# Revit family: Casement_38_E_Side_Hung_Standard
name_source: partatom
category: Windows
revit_build: Autodesk Revit 2014 (Build: 20130308_1515(x64)
units: mm (PartAtom-declared; Revit-internal decimal feet)

## types (18) — shared parameters
Aluminium Thickness = 1 mm  [stored 0.00328084 ft]
Area Pane Left Top = 0.52 m²
Bead SG Gap = 13 mm  [stored 0.0426509 ft]
Casement Dimension = 38 mm  [stored 0.124672 ft]
Custom Sash Height = 1154 mm  [stored 3.78609 ft]
Custom Sash Width = 554 mm  [stored 1.81759 ft]
DG Extrusion Start = 9 mm  [stored 0.0295276 ft]
DG Gasket Finish = Double Glazing Gasket Material
DG Thickness Calc = 4 mm  [stored 0.0131234 ft]
Default Sill Height = 800 mm  [stored 2.62467 ft]
Depth Bead = 24 mm  [stored 0.0787402 ft]
Description = Window 38mm, Type E side hung
Frame Center Offset = 19 mm  [stored 0.062336 ft]
Height Panel 1 = 1139 mm  [stored 3.73688 ft]
Height Sash = 1124 mm  [stored 3.68766 ft]
Height Sash Opening = 1154 mm  [stored 3.78609 ft]
Length Transom = 540 mm  [stored 1.77165 ft]
Limit Fixed Pane Height Max = 1800 mm
Limit Fixed Pane Height Min = 200 mm  [stored 0.656168 ft]
Limit Fixed Pane Width Max = 1500 mm
Limit Fixed Pane Width Min = 200 mm  [stored 0.656168 ft]
Limit Sash Height Max = 1500 mm
Limit Sash Height Min = 300 mm  [stored 0.984252 ft]
Limit Sash Width Max = 700 mm  [stored 2.29659 ft]
Limit Sash Width Min = 300 mm  [stored 0.984252 ft]
Limit Window Height Max = 1860 mm
Limit Window Height Min = 1430 mm
Limit Window Width Max = 2130 mm
Limit Window Width Min = 830 mm  [stored 2.7231 ft]
Manufacturer = Crealco
Max System DG One Piece Thickness = 6 mm  [stored 0.019685 ft]
Max System DG Unit Thickness = 25 mm  [stored 0.082021 ft]
Model = Casement 38
Offset Bead SG Center Reversed = 19 mm  [stored 0.062336 ft]
Offset Mullion Left = 570 mm  [stored 1.87008 ft]
Offset Panel 3 Bead Top = 1200 mm
Offset Panel 4 Left = 600 mm  [stored 1.9685 ft]
Offset Sash Left = 23 mm  [stored 0.0754593 ft]
Offset Sash Top = 23 mm  [stored 0.0754593 ft]
Offset Transom Top = 1170 mm
Offset Window Exterior = 19 mm  [stored 0.062336 ft]
SG Gasket Thickness = 6 mm  [stored 0.019685 ft]
Sash Center Offset = 16 mm  [stored 0.0524934 ft]
Sash Overlap = 7 mm  [stored 0.0229659 ft]
Sash Spacing Inner = 8 mm  [stored 0.0262467 ft]
URL = http://www.crealco.co.za
Wall Closure = By host
Width Bead = 15 mm  [stored 0.0492126 ft]
Width Fixed Pane Bottom LHS = 540 mm  [stored 1.77165 ft]
Width Panel 1 = 540 mm  [stored 1.77165 ft]
Width Profile = 30 mm  [stored 0.0984252 ft]
Width Sash = 524 mm  [stored 1.71916 ft]
Width Sash Opening = 554 mm  [stored 1.81759 ft]
zero-valued in all types: Window Exterior Offset

## per-type parameters (varying)
- 38-0915S-1000Pa: Area Pane Left Bottom=0.13 m²; Area Pane Right=0.36 m²; Clearvue Insulated LowE SHGC Value=0.51; Clearvue Insulated LowE U Value=3.91; Clearvue Insulated SHGC Value=0.56; Clearvue Insulated U Value=4.43; Clearvue SHGC Value=0.641; Clearvue U Value=6.69; Custom Windload=1000 mm  [stored 3.28084 ft]; Custom Window Height=1490 mm; Custom Window Width=890 mm  [stored 2.91995 ft]; Depth Mullion=39 mm  [stored 0.127953 ft]; Energy Advantage SHGC Value=0.576; Energy Advantage U Value=5.11; Height=1490 mm; Height Fixed Pane Bottom LHS=260 mm  [stored 0.853018 ft]; Height Fixed Pane RHS=1430 mm; Intruderprufe Insulated LowE SHGC Value=0.474; Intruderprufe Insulated LowE U Value=3.82; Intruderprufe Insulated SHGC Value=0.519; Intruderprufe Insulated U Value=4.32; Intruderprufe LowE SHGC Value=0.53; Intruderprufe LowE U Value=4.98; Intruderprufe SHGC Value=0.628; Intruderprufe U Value=6.75; Length Mullion=1490 mm; Max Pane Area=0.52 m²; Mullion Depth Windload Based=39 mm  [stored 0.127953 ft]; Width=890 mm  [stored 2.91995 ft]; Width Fixed Pane RHS=260 mm  [stored 0.853018 ft]; Windload Design=1000 mm  [stored 3.28084 ft]
- 38-0915S-1500Pa: Area Pane Left Bottom=0.13 m²; Area Pane Right=0.36 m²; Clearvue Insulated LowE SHGC Value=0.511; Clearvue Insulated LowE U Value=3.98; Clearvue Insulated SHGC Value=0.561; Clearvue Insulated U Value=45; Clearvue SHGC Value=0.64; Clearvue U Value=6.69; Custom Windload=1500 mm; Custom Window Height=1490 mm; Custom Window Width=890 mm  [stored 2.91995 ft]; Depth Mullion=54 mm  [stored 0.177165 ft]; Energy Advantage SHGC Value=0.574; Energy Advantage U Value=5.2; Height=1490 mm; Height Fixed Pane Bottom LHS=260 mm  [stored 0.853018 ft]; Height Fixed Pane RHS=1430 mm; Intruderprufe Insulated LowE SHGC Value=0.476; Intruderprufe Insulated LowE U Value=3.89; Intruderprufe Insulated SHGC Value=0.522; Intruderprufe Insulated U Value=4.39; Intruderprufe LowE SHGC Value=0.541; Intruderprufe LowE U Value=5.07; Intruderprufe SHGC Value=0.61; Intruderprufe U Value=6.59; Length Mullion=1490 mm; Max Pane Area=0.52 m²; Mullion Depth Windload Based=54 mm  [stored 0.177165 ft]; Width=890 mm  [stored 2.91995 ft]; Width Fixed Pane RHS=260 mm  [stored 0.853018 ft]; Windload Design=1500 mm
- 38-0915S-2000Pa: Area Pane Left Bottom=0.13 m²; Area Pane Right=0.36 m²; Clearvue Insulated LowE SHGC Value=0.511; Clearvue Insulated LowE U Value=3.98; Clearvue Insulated SHGC Value=0.561; Clearvue Insulated U Value=45; Clearvue SHGC Value=0.64; Clearvue U Value=6.69; Custom Windload=2000 mm; Custom Window Height=1490 mm; Custom Window Width=890 mm  [stored 2.91995 ft]; Depth Mullion=54 mm  [stored 0.177165 ft]; Energy Advantage SHGC Value=0.574; Energy Advantage U Value=5.2; Height=1490 mm; Height Fixed Pane Bottom LHS=260 mm  [stored 0.853018 ft]; Height Fixed Pane RHS=1430 mm; Intruderprufe Insulated LowE SHGC Value=0.476; Intruderprufe Insulated LowE U Value=3.89; Intruderprufe Insulated SHGC Value=0.522; Intruderprufe Insulated U Value=4.39; Intruderprufe LowE SHGC Value=0.541; Intruderprufe LowE U Value=5.07; Intruderprufe SHGC Value=0.61; Intruderprufe U Value=6.59; Length Mullion=1490 mm; Max Pane Area=0.52 m²; Mullion Depth Windload Based=54 mm  [stored 0.177165 ft]; Width=890 mm  [stored 2.91995 ft]; Width Fixed Pane RHS=260 mm  [stored 0.853018 ft]; Windload Design=2000 mm
- 38-1215S-1000Pa: Area Pane Left Bottom=0.13 m²; Area Pane Right=0.78 m²; Clearvue Insulated LowE SHGC Value=0.575; Clearvue Insulated LowE U Value=3.67; Clearvue Insulated SHGC Value=0.632; Clearvue Insulated U Value=4.28; Clearvue SHGC Value=0.722; Clearvue U Value=6.86; Custom Windload=1000 mm  [stored 3.28084 ft]; Custom Window Height=1490 mm; Custom Window Width=1190 mm  [stored 3.9042 ft]; Depth Mullion=39 mm  [stored 0.127953 ft]; Energy Advantage SHGC Value=0.647; Energy Advantage U Value=5.06; Height=1490 mm; Height Fixed Pane Bottom LHS=260 mm  [stored 0.853018 ft]; Height Fixed Pane RHS=1430 mm; Intruderprufe Insulated LowE SHGC Value=0.532; Intruderprufe Insulated LowE U Value=3.59; Intruderprufe Insulated SHGC Value=0.585; Intruderprufe Insulated U Value=4.18; Intruderprufe LowE SHGC Value=0.604; Intruderprufe LowE U Value=4.94; Intruderprufe SHGC Value=0.698; Intruderprufe U Value=6.73; Length Mullion=1490 mm; Max Pane Area=0.78 m²; Mullion Depth Windload Based=39 mm  [stored 0.127953 ft]; Width=1190 mm  [stored 3.9042 ft]; Width Fixed Pane RHS=560 mm; Windload Design=1000 mm  [stored 3.28084 ft]
- 38-1215S-1500Pa: Area Pane Left Bottom=0.13 m²; Area Pane Right=0.78 m²; Clearvue Insulated LowE SHGC Value=0.575; Clearvue Insulated LowE U Value=3.75; Clearvue Insulated SHGC Value=0.632; Clearvue Insulated U Value=4.34; Clearvue SHGC Value=0.721; Clearvue U Value=6.85; Custom Windload=1500 mm; Custom Window Height=1490 mm; Custom Window Width=1190 mm  [stored 3.9042 ft]; Depth Mullion=54 mm  [stored 0.177165 ft]; Energy Advantage SHGC Value=0.645; Energy Advantage U Value=5.13; Height=1490 mm; Height Fixed Pane Bottom LHS=260 mm  [stored 0.853018 ft]; Height Fixed Pane RHS=1430 mm; Intruderprufe Insulated LowE SHGC Value=0.534; Intruderprufe Insulated LowE U Value=3.65; Intruderprufe Insulated SHGC Value=0.587; Intruderprufe Insulated U Value=4.23; Intruderprufe LowE SHGC Value=0.606; Intruderprufe LowE U Value=5.01; Intruderprufe SHGC Value=0.685; Intruderprufe U Value=6.75; Length Mullion=1490 mm; Max Pane Area=0.78 m²; Mullion Depth Windload Based=54 mm  [stored 0.177165 ft]; Width=1190 mm  [stored 3.9042 ft]; Width Fixed Pane RHS=560 mm; Windload Design=1500 mm
- 38-1215S-2000Pa: Area Pane Left Bottom=0.13 m²; Area Pane Right=0.78 m²; Clearvue Insulated LowE SHGC Value=0.575; Clearvue Insulated LowE U Value=3.75; Clearvue Insulated SHGC Value=0.632; Clearvue Insulated U Value=4.34; Clearvue SHGC Value=0.721; Clearvue U Value=6.85; Custom Windload=2000 mm; Custom Window Height=1490 mm; Custom Window Width=1190 mm  [stored 3.9042 ft]; Depth Mullion=54 mm  [stored 0.177165 ft]; Energy Advantage SHGC Value=0.645; Energy Advantage U Value=5.13; Height=1490 mm; Height Fixed Pane Bottom LHS=260 mm  [stored 0.853018 ft]; Height Fixed Pane RHS=1430 mm; Intruderprufe Insulated LowE SHGC Value=0.534; Intruderprufe Insulated LowE U Value=3.65; Intruderprufe Insulated SHGC Value=0.587; Intruderprufe Insulated U Value=4.23; Intruderprufe LowE SHGC Value=0.606; Intruderprufe LowE U Value=5.01; Intruderprufe SHGC Value=0.685; Intruderprufe U Value=6.75; Length Mullion=1490 mm; Max Pane Area=0.78 m²; Mullion Depth Windload Based=54 mm  [stored 0.177165 ft]; Width=1190 mm  [stored 3.9042 ft]; Width Fixed Pane RHS=560 mm; Windload Design=2000 mm
- 38-1515S-1000Pa: Area Pane Left Bottom=0.13 m²; Area Pane Right=1.21 m²; Clearvue Insulated LowE SHGC Value=0.616; Clearvue Insulated LowE U Value=3.51; Clearvue Insulated SHGC Value=0.677; Clearvue Insulated U Value=4.19; Clearvue SHGC Value=0.772; Clearvue U Value=6.96; Custom Windload=1000 mm  [stored 3.28084 ft]; Custom Window Height=1490 mm; Custom Window Width=1490 mm; Depth Mullion=39 mm  [stored 0.127953 ft]; Energy Advantage SHGC Value=0.692; Energy Advantage U Value=5.03; Height=1490 mm; Height Fixed Pane Bottom LHS=260 mm  [stored 0.853018 ft]; Height Fixed Pane RHS=1430 mm; Intruderprufe Insulated LowE SHGC Value=0.569; Intruderprufe Insulated LowE U Value=3.44; Intruderprufe Insulated SHGC Value=0.626; Intruderprufe Insulated U Value=4.09; Intruderprufe LowE SHGC Value=0.646; Intruderprufe LowE U Value=4.91; Intruderprufe SHGC Value=0.743; Intruderprufe U Value=6.83; Length Mullion=1490 mm; Max Pane Area=1.21 m²; Mullion Depth Windload Based=39 mm  [stored 0.127953 ft]; Width=1490 mm; Width Fixed Pane RHS=860 mm  [stored 2.82152 ft]; Windload Design=1000 mm  [stored 3.28084 ft]
- 38-1515S-1500Pa: Area Pane Left Bottom=0.13 m²; Area Pane Right=1.21 m²; Clearvue Insulated LowE SHGC Value=0.616; Clearvue Insulated LowE U Value=3.56; Clearvue Insulated SHGC Value=0.677; Clearvue Insulated U Value=4.23; Clearvue SHGC Value=0.772; Clearvue U Value=6.69; Custom Windload=1500 mm; Custom Window Height=1490 mm; Custom Window Width=1490 mm; Depth Mullion=54 mm  [stored 0.177165 ft]; Energy Advantage SHGC Value=0.691; Energy Advantage U Value=5.09; Height=1490 mm; Height Fixed Pane Bottom LHS=260 mm  [stored 0.853018 ft]; Height Fixed Pane RHS=1430 mm; Intruderprufe Insulated LowE SHGC Value=0.57; Intruderprufe Insulated LowE U Value=3.49; Intruderprufe Insulated SHGC Value=0.629; Intruderprufe Insulated U Value=4.13; Intruderprufe LowE SHGC Value=0.647; Intruderprufe LowE U Value=4.97; Intruderprufe SHGC Value=0.732; Intruderprufe U Value=6.84; Length Mullion=1490 mm; Max Pane Area=1.21 m²; Mullion Depth Windload Based=54 mm  [stored 0.177165 ft]; Width=1490 mm; Width Fixed Pane RHS=860 mm  [stored 2.82152 ft]; Windload Design=1500 mm
- 38-1515S-2000Pa: Area Pane Left Bottom=0.13 m²; Area Pane Right=1.21 m²; Clearvue Insulated LowE SHGC Value=0.616; Clearvue Insulated LowE U Value=3.56; Clearvue Insulated SHGC Value=0.677; Clearvue Insulated U Value=4.23; Clearvue SHGC Value=0.772; Clearvue U Value=6.69; Custom Windload=2000 mm; Custom Window Height=1490 mm; Custom Window Width=1490 mm; Depth Mullion=54 mm  [stored 0.177165 ft]; Energy Advantage SHGC Value=0.691; Energy Advantage U Value=5.09; Height=1490 mm; Height Fixed Pane Bottom LHS=260 mm  [stored 0.853018 ft]; Height Fixed Pane RHS=1430 mm; Intruderprufe Insulated LowE SHGC Value=0.57; Intruderprufe Insulated LowE U Value=3.49; Intruderprufe Insulated SHGC Value=0.629; Intruderprufe Insulated U Value=4.13; Intruderprufe LowE SHGC Value=0.647; Intruderprufe LowE U Value=4.97; Intruderprufe SHGC Value=0.732; Intruderprufe U Value=6.84; Length Mullion=1490 mm; Max Pane Area=1.21 m²; Mullion Depth Windload Based=54 mm  [stored 0.177165 ft]; Width=1490 mm; Width Fixed Pane RHS=860 mm  [stored 2.82152 ft]; Windload Design=2000 mm
- 38-0918S-1000Pa: Area Pane Left Bottom=0.29 m²; Area Pane Right=0.43 m²; Clearvue Insulated LowE SHGC Value=0.55; Clearvue Insulated LowE U Value=4.07; Clearvue Insulated SHGC Value=0.604; Clearvue Insulated U Value=4.64; Clearvue SHGC Value=0.688; Clearvue U Value=7; Custom Windload=1000 mm  [stored 3.28084 ft]; Custom Window Height=1790 mm; Custom Window Width=890 mm  [stored 2.91995 ft]; Depth Mullion=54 mm  [stored 0.177165 ft]; Energy Advantage SHGC Value=0.617; Energy Advantage U Value=5.38; Height=1790 mm; Height Fixed Pane Bottom LHS=560 mm; Height Fixed Pane RHS=1730 mm; Intruderprufe Insulated LowE SHGC Value=0.512; Intruderprufe Insulated LowE U Value=3.98; Intruderprufe Insulated SHGC Value=0.562; Intruderprufe Insulated U Value=4.52; Intruderprufe LowE SHGC Value=0.581; Intruderprufe LowE U Value=5.25; Intruderprufe SHGC Value=0.655; Intruderprufe U Value=6.9; Length Mullion=1790 mm; Max Pane Area=0.52 m²; Mullion Depth Windload Based=54 mm  [stored 0.177165 ft]; Width=890 mm  [stored 2.91995 ft]; Width Fixed Pane RHS=260 mm  [stored 0.853018 ft]; Windload Design=1000 mm  [stored 3.28084 ft]
- 38-0918S-1500Pa: Area Pane Left Bottom=0.29 m²; Area Pane Right=0.43 m²; Clearvue Insulated LowE SHGC Value=0.55; Clearvue Insulated LowE U Value=4.07; Clearvue Insulated SHGC Value=0.604; Clearvue Insulated U Value=4.64; Clearvue SHGC Value=0.688; Clearvue U Value=7; Custom Windload=1500 mm; Custom Window Height=1790 mm; Custom Window Width=890 mm  [stored 2.91995 ft]; Depth Mullion=54 mm  [stored 0.177165 ft]; Energy Advantage SHGC Value=0.617; Energy Advantage U Value=5.38; Height=1790 mm; Height Fixed Pane Bottom LHS=560 mm; Height Fixed Pane RHS=1730 mm; Intruderprufe Insulated LowE SHGC Value=0.512; Intruderprufe Insulated LowE U Value=3.98; Intruderprufe Insulated SHGC Value=0.562; Intruderprufe Insulated U Value=4.52; Intruderprufe LowE SHGC Value=0.581; Intruderprufe LowE U Value=5.25; Intruderprufe SHGC Value=0.655; Intruderprufe U Value=6.9; Length Mullion=1790 mm; Max Pane Area=0.52 m²; Mullion Depth Windload Based=54 mm  [stored 0.177165 ft]; Width=890 mm  [stored 2.91995 ft]; Width Fixed Pane RHS=260 mm  [stored 0.853018 ft]; Windload Design=1500 mm
- 38-0918S-2000Pa: Area Pane Left Bottom=0.29 m²; Area Pane Right=0.43 m²; Clearvue Insulated LowE SHGC Value=0.552; Clearvue Insulated LowE U Value=4.2; Clearvue Insulated SHGC Value=0.606; Clearvue Insulated U Value=4.76; Clearvue SHGC Value=0.688; Clearvue U Value=6.9; Custom Windload=2000 mm; Custom Window Height=1790 mm; Custom Window Width=890 mm  [stored 2.91995 ft]; Depth Mullion=70 mm  [stored 0.229659 ft]; Energy Advantage SHGC Value=0.619; Energy Advantage U Value=5.54; Height=1790 mm; Height Fixed Pane Bottom LHS=560 mm; Height Fixed Pane RHS=1730 mm; Intruderprufe Insulated LowE SHGC Value=0.513; Intruderprufe Insulated LowE U Value=4.1; Intruderprufe Insulated SHGC Value=0.562; Intruderprufe Insulated U Value=4.64; Intruderprufe LowE SHGC Value=0.581; Intruderprufe LowE U Value=5.41; Intruderprufe SHGC Value=0.64; Intruderprufe U Value=6.92; Length Mullion=1790 mm; Max Pane Area=0.52 m²; Mullion Depth Windload Based=70 mm  [stored 0.229659 ft]; Width=890 mm  [stored 2.91995 ft]; Width Fixed Pane RHS=260 mm  [stored 0.853018 ft]; Windload Design=2000 mm
- 38-1218S-1000Pa: Area Pane Left Bottom=0.29 m²; Area Pane Right=0.95 m²; Clearvue Insulated LowE SHGC Value=0.634; Clearvue Insulated LowE U Value=3.92; Clearvue Insulated SHGC Value=0.697; Clearvue Insulated U Value=4.6; Clearvue SHGC Value=0.795; Clearvue U Value=7.39; Custom Windload=1000 mm  [stored 3.28084 ft]; Custom Window Height=1790 mm; Custom Window Width=1190 mm  [stored 3.9042 ft]; Depth Mullion=54 mm  [stored 0.177165 ft]; Energy Advantage SHGC Value=0.711; Energy Advantage U Value=5.47; Height=1790 mm; Height Fixed Pane Bottom LHS=560 mm; Height Fixed Pane RHS=1730 mm; Intruderprufe Insulated LowE SHGC Value=0.588; Intruderprufe Insulated LowE U Value=3.84; Intruderprufe Insulated SHGC Value=0.647; Intruderprufe Insulated U Value=4.49; Intruderprufe LowE SHGC Value=0.667; Intruderprufe LowE U Value=5.34; Intruderprufe SHGC Value=0.754; Intruderprufe U Value=7.27; Length Mullion=1790 mm; Max Pane Area=0.95 m²; Mullion Depth Windload Based=54 mm  [stored 0.177165 ft]; Width=1190 mm  [stored 3.9042 ft]; Width Fixed Pane RHS=560 mm; Windload Design=1000 mm  [stored 3.28084 ft]
- 38-1218S-1500Pa: Area Pane Left Bottom=0.29 m²; Area Pane Right=0.95 m²; Clearvue Insulated LowE SHGC Value=0.636; Clearvue Insulated LowE U Value=4.02; Clearvue Insulated SHGC Value=0.699; Clearvue Insulated U Value=4.7; Clearvue SHGC Value=0.794; Clearvue U Value=7.3; Custom Windload=1500 mm; Custom Window Height=1790 mm; Custom Window Width=1190 mm  [stored 3.9042 ft]; Depth Mullion=70 mm  [stored 0.229659 ft]; Energy Advantage SHGC Value=0.713; Energy Advantage U Value=5.6; Height=1790 mm; Height Fixed Pane Bottom LHS=560 mm; Height Fixed Pane RHS=1730 mm; Intruderprufe Insulated LowE SHGC Value=0.589; Intruderprufe Insulated LowE U Value=3.93; Intruderprufe Insulated SHGC Value=0.648; Intruderprufe Insulated U Value=4.58; Intruderprufe LowE SHGC Value=0.668; Intruderprufe LowE U Value=5.47; Intruderprufe SHGC Value=0.741; Intruderprufe U Value=7.28; Length Mullion=1790 mm; Max Pane Area=0.95 m²; Mullion Depth Windload Based=70 mm  [stored 0.229659 ft]; Width=1190 mm  [stored 3.9042 ft]; Width Fixed Pane RHS=560 mm; Windload Design=1500 mm
- 38-1218S-2000Pa: Area Pane Left Bottom=0.29 m²; Area Pane Right=0.95 m²; Clearvue Insulated LowE SHGC Value=0.636; Clearvue Insulated LowE U Value=4.02; Clearvue Insulated SHGC Value=0.699; Clearvue Insulated U Value=4.7; Clearvue SHGC Value=0.794; Clearvue U Value=7.3; Custom Windload=2000 mm; Custom Window Height=1790 mm; Custom Window Width=1190 mm  [stored 3.9042 ft]; Depth Mullion=70 mm  [stored 0.229659 ft]; Energy Advantage SHGC Value=0.713; Energy Advantage U Value=5.6; Height=1790 mm; Height Fixed Pane Bottom LHS=560 mm; Height Fixed Pane RHS=1730 mm; Intruderprufe Insulated LowE SHGC Value=0.589; Intruderprufe Insulated LowE U Value=3.93; Intruderprufe Insulated SHGC Value=0.648; Intruderprufe Insulated U Value=4.58; Intruderprufe LowE SHGC Value=0.668; Intruderprufe LowE U Value=5.47; Intruderprufe SHGC Value=0.741; Intruderprufe U Value=7.28; Length Mullion=1790 mm; Max Pane Area=0.95 m²; Mullion Depth Windload Based=70 mm  [stored 0.229659 ft]; Width=1190 mm  [stored 3.9042 ft]; Width Fixed Pane RHS=560 mm; Windload Design=2000 mm
- 38-1518S-1000Pa: Area Pane Left Bottom=0.29 m²; Area Pane Right=1.46 m²; Clearvue Insulated LowE SHGC Value=0.691; Clearvue Insulated LowE U Value=3.82; Clearvue Insulated SHGC Value=0.759; Clearvue Insulated U Value=4.58; Clearvue SHGC Value=0; Clearvue U Value=7.9; Custom Windload=1000 mm  [stored 3.28084 ft]; Custom Window Height=1790 mm; Custom Window Width=1490 mm; Depth Mullion=54 mm  [stored 0.177165 ft]; Energy Advantage SHGC Value=0; Energy Advantage U Value=7.9; Height=1790 mm; Height Fixed Pane Bottom LHS=560 mm; Height Fixed Pane RHS=1730 mm; Intruderprufe Insulated LowE SHGC Value=0.639; Intruderprufe Insulated LowE U Value=3.74; Intruderprufe Insulated SHGC Value=0.704; Intruderprufe Insulated U Value=4.47; Intruderprufe LowE SHGC Value=0.725; Intruderprufe LowE U Value=5.4; Intruderprufe SHGC Value=0.819; Intruderprufe U Value=7.51; Length Mullion=1790 mm; Max Pane Area=1.46 m²; Mullion Depth Windload Based=54 mm  [stored 0.177165 ft]; Width=1490 mm; Width Fixed Pane RHS=860 mm  [stored 2.82152 ft]; Windload Design=1000 mm  [stored 3.28084 ft]
- 38-1518S-1500Pa: Area Pane Left Bottom=0.29 m²; Area Pane Right=1.46 m²; Clearvue Insulated LowE SHGC Value=0.692; Clearvue Insulated LowE U Value=3.9; Clearvue Insulated SHGC Value=0.761; Clearvue Insulated U Value=4.66; Clearvue SHGC Value=0; Clearvue U Value=7.9; Custom Windload=1500 mm; Custom Window Height=1790 mm; Custom Window Width=1490 mm; Depth Mullion=70 mm  [stored 0.229659 ft]; Energy Advantage SHGC Value=0; Energy Advantage U Value=7.9; Height=1790 mm; Height Fixed Pane Bottom LHS=560 mm; Height Fixed Pane RHS=1730 mm; Intruderprufe Insulated LowE SHGC Value=0.639; Intruderprufe Insulated LowE U Value=3.82; Intruderprufe Insulated SHGC Value=0.705; Intruderprufe Insulated U Value=4.55; Intruderprufe LowE SHGC Value=0.725; Intruderprufe LowE U Value=5.51; Intruderprufe SHGC Value=0.809; Intruderprufe U Value=7.52; Length Mullion=1790 mm; Max Pane Area=1.46 m²; Mullion Depth Windload Based=70 mm  [stored 0.229659 ft]; Width=1490 mm; Width Fixed Pane RHS=860 mm  [stored 2.82152 ft]; Windload Design=1500 mm
- 38-1518S-2000Pa: Area Pane Left Bottom=0.29 m²; Area Pane Right=1.46 m²; Clearvue Insulated LowE SHGC Value=0.692; Clearvue Insulated LowE U Value=3.9; Clearvue Insulated SHGC Value=0.761; Clearvue Insulated U Value=4.66; Clearvue SHGC Value=0; Clearvue U Value=7.9; Custom Windload=2000 mm; Custom Window Height=1790 mm; Custom Window Width=1490 mm; Depth Mullion=70 mm  [stored 0.229659 ft]; Energy Advantage SHGC Value=0; Energy Advantage U Value=7.9; Height=1790 mm; Height Fixed Pane Bottom LHS=560 mm; Height Fixed Pane RHS=1730 mm; Intruderprufe Insulated LowE SHGC Value=0.639; Intruderprufe Insulated LowE U Value=3.82; Intruderprufe Insulated SHGC Value=0.705; Intruderprufe Insulated U Value=4.55; Intruderprufe LowE SHGC Value=0.725; Intruderprufe LowE U Value=5.51; Intruderprufe SHGC Value=0.809; Intruderprufe U Value=7.52; Length Mullion=1790 mm; Max Pane Area=1.46 m²; Mullion Depth Windload Based=70 mm  [stored 0.229659 ft]; Width=1490 mm; Width Fixed Pane RHS=860 mm  [stored 2.82152 ft]; Windload Design=2000 mm

note: [stored X ft] marks values corroborated as IEEE doubles in the binary element streams (Revit-internal decimal feet)

## geometry (parser evidence)
native form markers: Blend x4, Extrusion x1, Sweep x28
no freeform markers — native parametric forms only
